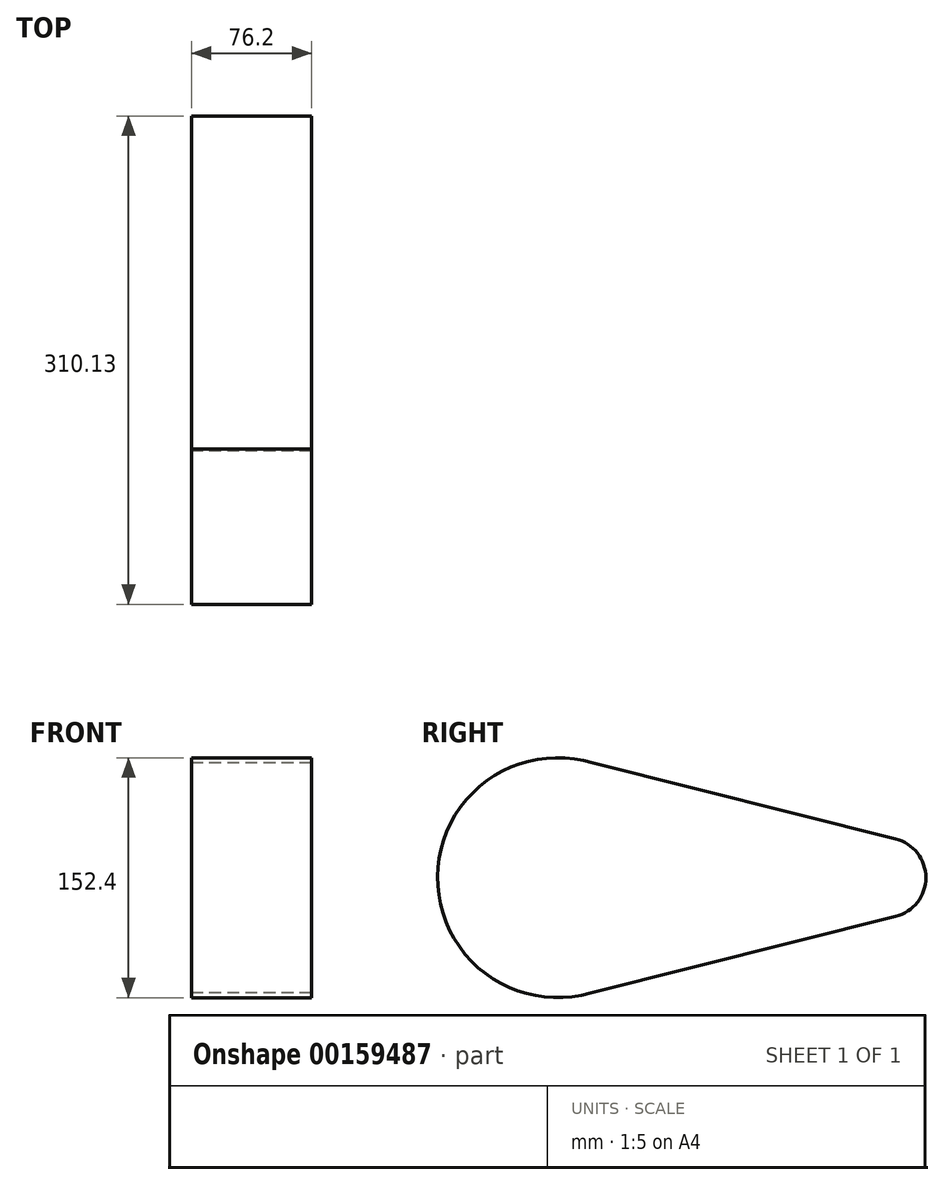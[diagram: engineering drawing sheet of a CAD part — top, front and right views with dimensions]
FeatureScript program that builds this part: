
annotation { "Feature Type Name" : "Feature", "Feature Type Description" : "" }
export const myFeature = defineFeature(function(context is Context, id is Id, definition is map)
    precondition{}
    {
        {
            var Q0;
            Q0=qCreatedBy(makeId("Right.planeOp"),FACE);
            var sketch = newSketch(context, id + "F0", { "sketchPlane" : qUnion([Q0])});
            skCircle(sketch, "E0", {"center": v(0, 0) * mm, "radius": 76.2 * mm});
            skCircle(sketch, "E1", {"center": v(208.53, 0) * mm, "radius": 25.4 * mm});
            skLineSegment(sketch, "E2", {"start": v(14.9, 74.7) * mm, "end": v(214.7, 24.64) * mm});
            skLineSegment(sketch, "E3", {"start": v(16.15, -74.46) * mm, "end": v(214.7, -24.64) * mm});
            skSolve(sketch);
        }
        {
            var Q0;
            {var subQ0=sQuery(id+"F0.wireOp",EDGE,"E2");var subQ1=sQuery(id+"F0.wireOp",EDGE,"E0");var subQ2=makeQuery(id+"F0.imprint","INTERSECT",VERTEX,{"disambiguationData":[OD(0.0)],"derivedFrom":[subQ1,subQ0]});Q0=makeQuery(id+"F0.imprint","IMPRINT",FACE,{"disambiguationData":[TD([[makeQuery(id+"F0.imprint","IMPRINT",EDGE,{"disambiguationData":[TD([[subQ2,-1.0]])],"derivedFrom":subQ1}),1.0]])]});}
            var Q1;
            {var subQ0=sQuery(id+"F0.wireOp",EDGE,"E1");var subQ1=makeQuery(id+"F0.imprint","INTERSECT",VERTEX,{"derivedFrom":[subQ0,sQuery(id+"F0.wireOp",EDGE,"E2")]});Q1=makeQuery(id+"F0.imprint","IMPRINT",FACE,{"disambiguationData":[TD([[makeQuery(id+"F0.imprint","IMPRINT",EDGE,{"disambiguationData":[TD([[subQ1,-1.0]])],"derivedFrom":subQ0}),1.0]])]});}
            var Q2;
            {var subQ0=sQuery(id+"F0.wireOp",EDGE,"E2");var subQ1=sQuery(id+"F0.wireOp",EDGE,"E0");var subQ2=makeQuery(id+"F0.imprint","INTERSECT",VERTEX,{"disambiguationData":[OD(1.0)],"derivedFrom":[subQ1,subQ0]});Q2=makeQuery(id+"F0.imprint","IMPRINT",FACE,{"disambiguationData":[TD([[makeQuery(id+"F0.imprint","IMPRINT",EDGE,{"disambiguationData":[TD([[subQ2,1.0]])],"derivedFrom":subQ1}),-1.0]])]});}
            var Q3;
            {var subQ0=sQuery(id+"F0.wireOp",EDGE,"E3");var subQ1=sQuery(id+"F0.wireOp",EDGE,"E0");var subQ2=makeQuery(id+"F0.imprint","INTERSECT",VERTEX,{"disambiguationData":[OD(0.0)],"derivedFrom":[subQ1,subQ0]});Q3=makeQuery(id+"F0.imprint","IMPRINT",FACE,{"disambiguationData":[TD([[makeQuery(id+"F0.imprint","IMPRINT",EDGE,{"disambiguationData":[TD([[subQ2,-1.0]])],"derivedFrom":subQ1}),1.0]])]});}
            var Q4;
            {var subQ0=sQuery(id+"F0.wireOp",EDGE,"E2");var subQ1=sQuery(id+"F0.wireOp",EDGE,"E0");var subQ2=makeQuery(id+"F0.imprint","INTERSECT",VERTEX,{"disambiguationData":[OD(0.0)],"derivedFrom":[subQ1,subQ0]});Q4=makeQuery(id+"F0.imprint","IMPRINT",FACE,{"disambiguationData":[TD([[makeQuery(id+"F0.imprint","IMPRINT",EDGE,{"disambiguationData":[TD([[subQ2,1.0]])],"derivedFrom":subQ1}),1.0]])]});}
            extrude(context, id + "F1", {"entities" : qUnion([Q0, Q1, Q2, Q3, Q4]), "depth" : 76.2 * mm});
        }
        {
            var Q0;
            Q0 = qSketchRegion(id + "F0", true);
            extrude(context, id + "F2", {"entities" : qUnion([Q0]), "operationType" : NewBodyOperationType.ADD, "depth" : 25 * mm});
        }
    });
